# Revit family: Sink-Top_Undermount-Kitchen-KOHLER-INDIO-K-3885T
name_source: partatom
category: Plumbing Fixtures
revit_build: Autodesk Revit 2017 (Build: 20160225_1515(x64)
units: mm (PartAtom-declared; Revit-internal decimal feet)

## family parameters
Cut with Voids When Loaded = No
Host = Face
OmniClass Number = 23.31.13.00
OmniClass Title = Sinks
Part Type = Normal
Room Calculation Point = No
Round Connector Dimension = Use Diameter
Shared = No

## types (6) — shared parameters
ADA Compliant = No
Assembly Code = D2010400
CW Connection = No
Cold Water Inlet = Cold Water Inlet
Date Modified = 11/03/2020
Default Elevation = 36"
Description = INDIO SMART One-size trough above/under counter dual purpose kitchen sink
Drain Included = Yes
HW Connection = No
Height = 8 11/16"
Height1 = 10 11/16"
Hot Water Inlet = Hot Water Inlet
Length = 18 7/8"
Manufacturer = KOHLER Co.
Master Format 2014 = 22 41 16
Master Format 2014 Name = Residential Lavatories and Sinks
Material = Cast Iron
Product Documentation Link = https://files.kohler.com.cn
Product Name = INDIO
Product Page URL = https://www.kohler.com.cn
URL = http://www.kohler.com.cn
Vent Connection = No
Waste Connection = Yes
Waste Water Outlet 1 = Waste Water Outlet 1
Waste Water Outlet 2 = Waste Water Outlet 2
WaterSense Certified = No
Width = 33 1/16"

## per-type parameters (varying)
| type | Finish | Model | Type |
| 0-White | KOHLER-Cast_Iron-0-White | K-3885T-1S-0 | 1 |
| 71-Pink Green | KOHLER-Cast_Iron-71-Pink_Green | K-3885T-1S-71 | 2 |
| 89-Pink | KOHLER-Cast_Iron-89-Pink | K-3885T-1S-89 | 3 |
| 52-Navy Blue | KOHLER-Cast_Iron-52-Navy_Blue | K-3885T-1S-52 | 4 |
| FF-Sea Salt | KOHLER-Enameled_Cast_Iron-FF-Sea_Salt | K-3885T-1S-FF | 5 |
| R1-Roussillon Red | KOHLER-Enameled_Cast_Iron-R1-Roussillon_Red | K-3885T-1S-R1 | 6 |

## geometry (parser evidence)
native form markers: Sweep x8
no freeform markers — native parametric forms only
